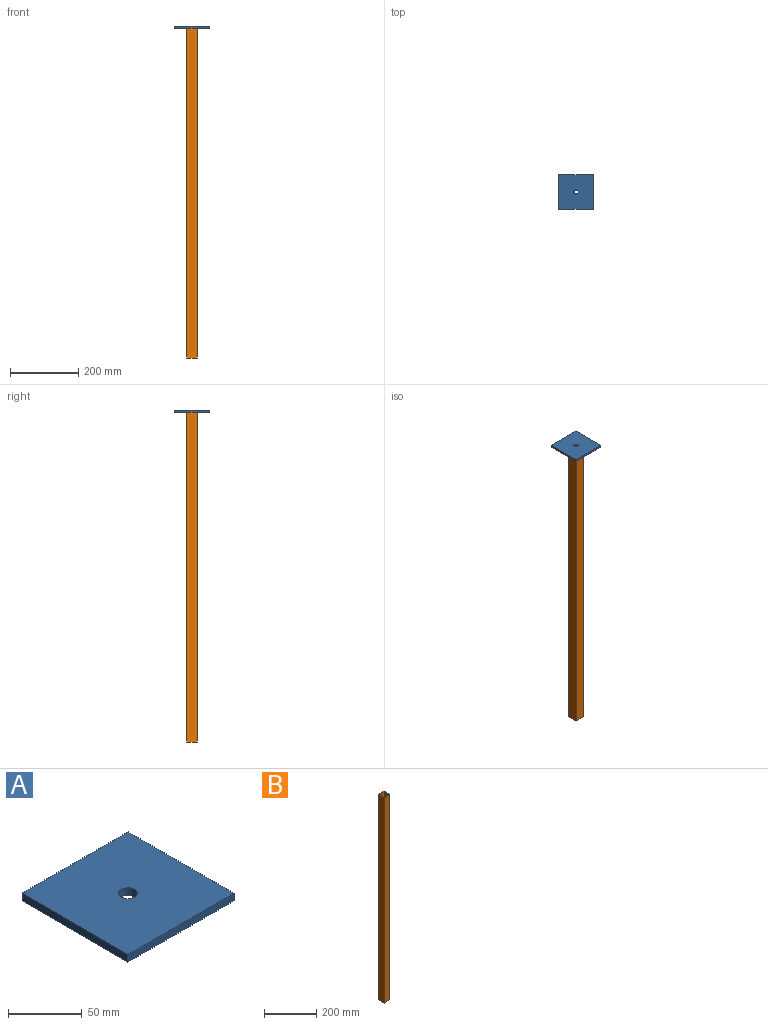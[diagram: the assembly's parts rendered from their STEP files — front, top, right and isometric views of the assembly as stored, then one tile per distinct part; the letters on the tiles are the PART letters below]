
ASSEMBLY  parts=2 mates=1
PART A: 7 faces, bbox 101.6x101.6x6.4 mm
  f0: plane 101.6x6.35mm, normal (0,-1,0), area 645.2mm2, adj f1,f4,f5,f6
  f1: plane 101.6x6.35mm, normal (1,0,0), area 645.2mm2, adj f0,f2,f5,f6
  f2: plane 101.6x6.35mm, normal (0,1,0), area 645.2mm2, adj f1,f4,f5,f6
  f3: cylinder r=6.35mm len=12.7mm, axis (0,0,-1), area 253.4mm2, adj f5,f6
  f4: plane 101.6x6.35mm, normal (-1,0,0), area 645.2mm2, adj f0,f2,f5,f6
  f5: plane 101.6x101.6mm, normal (0,0,1), area 10195.9mm2, adj f0,f1,f2,f3,f4
  f6: plane 101.6x101.6mm, normal (0,0,-1), area 10195.9mm2, adj f0,f1,f2,f3,f4
PART B: 10 faces, bbox 31.8x31.8x965.2 mm
  f0: plane 965.2x31.75mm, normal (0,1,0), area 30645.1mm2, adj f1,f7,f8,f9
  f1: plane 965.2x31.75mm, normal (-1,0,0), area 30645.1mm2, adj f0,f2,f8,f9
  f2: plane 965.2x31.75mm, normal (0,-1,0), area 30645.1mm2, adj f1,f7,f8,f9
  f3: plane 965.2x25.4mm, normal (-1,0,0), area 24516.1mm2, adj f4,f6,f8,f9
  f4: plane 965.2x25.4mm, normal (0,1,0), area 24516.1mm2, adj f3,f5,f8,f9
  f5: plane 965.2x25.4mm, normal (1,0,0), area 24516.1mm2, adj f4,f6,f8,f9
  f6: plane 965.2x25.4mm, normal (0,-1,0), area 24516.1mm2, adj f3,f5,f8,f9
  f7: plane 965.2x31.75mm, normal (1,0,0), area 30645.1mm2, adj f0,f2,f8,f9
  f8: plane 31.75x31.75mm, normal (0,0,1), area 362.9mm2, adj f0,f1,f2,f3,f4,f5,f6,f7
  f9: plane 31.75x31.75mm, normal (0,0,-1), area 362.9mm2, adj f0,f1,f2,f3,f4,f5,f6,f7
PLACE A t=(-425.44,-221.38,508.93)mm
PLACE B t=(-425.44,-221.38,-456.27)mm
MATE fastened B.f8 <-> A.f3  axis (0,0,1) through (-425.44,-221.38,508.93)mm
